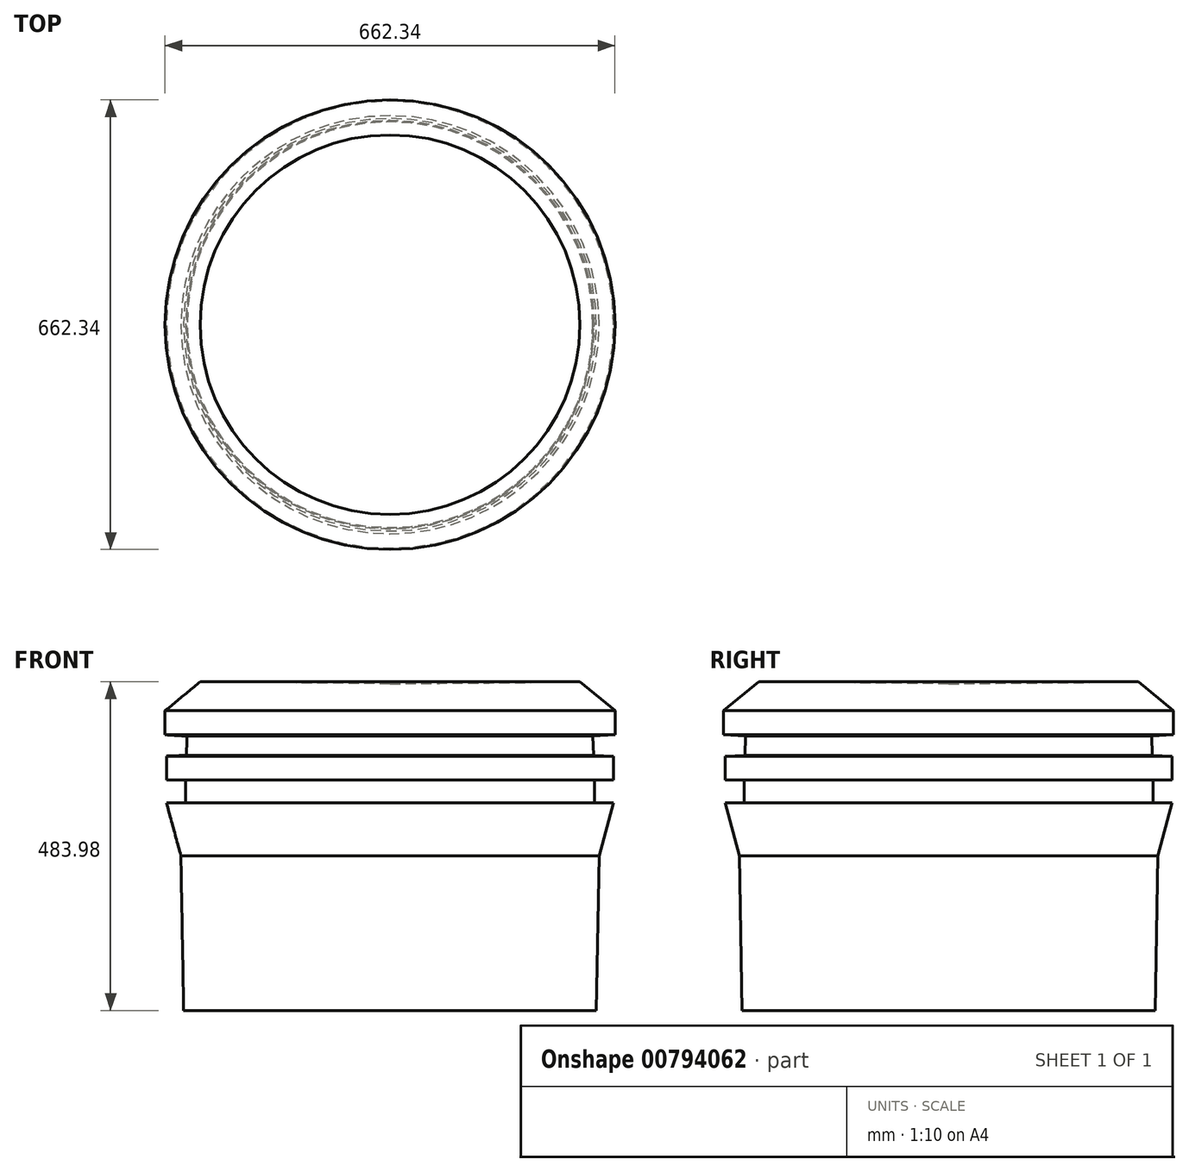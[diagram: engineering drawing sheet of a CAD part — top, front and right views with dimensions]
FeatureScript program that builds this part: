
annotation { "Feature Type Name" : "Feature", "Feature Type Description" : "" }
export const myFeature = defineFeature(function(context is Context, id is Id, definition is map)
    precondition{}
    {
        {
            var Q0;
            Q0=qCreatedBy(makeId("Front.planeOp"),FACE);
            var sketch = newSketch(context, id + "F0", { "sketchPlane" : qUnion([Q0])});
            skLineSegment(sketch, "E0", {"start": v(0, 0) * mm, "end": v(0, 295.8) * mm, "construction": true});
            skLineSegment(sketch, "E1", {"start": v(0, 0) * mm, "end": v(303.86, 0) * mm});
            skLineSegment(sketch, "E2", {"start": v(303.86, 0) * mm, "end": v(307.9, 228.01) * mm});
            skLineSegment(sketch, "E3", {"start": v(307.9, 228.01) * mm, "end": v(329.15, 305.92) * mm});
            skLineSegment(sketch, "E4", {"start": v(329.15, 305.92) * mm, "end": v(300.82, 305.92) * mm});
            skLineSegment(sketch, "E5", {"start": v(300.82, 305.92) * mm, "end": v(300.82, 339.3) * mm});
            skLineSegment(sketch, "E6", {"start": v(300.82, 339.3) * mm, "end": v(329.15, 339.3) * mm});
            skLineSegment(sketch, "E7", {"start": v(329.15, 339.3) * mm, "end": v(329.15, 374.71) * mm});
            skLineSegment(sketch, "E8", {"start": v(329.15, 374.71) * mm, "end": v(299.81, 375.73) * mm});
            skLineSegment(sketch, "E9", {"start": v(299.81, 375.73) * mm, "end": v(298.8, 404.05) * mm});
            skLineSegment(sketch, "E10", {"start": v(298.8, 404.05) * mm, "end": v(331.17, 406.08) * mm});
            skLineSegment(sketch, "E11", {"start": v(331.17, 406.08) * mm, "end": v(331.17, 441.49) * mm});
            skLineSegment(sketch, "E12", {"start": v(331.17, 441.49) * mm, "end": v(279.58, 483.98) * mm});
            skLineSegment(sketch, "E13", {"start": v(279.58, 483.98) * mm, "end": v(0, 481.2) * mm});
            skLineSegment(sketch, "E14", {"start": v(0, 0) * mm, "end": v(0, 481.2) * mm});
            skSolve(sketch);
        }
        {
            var Q0;
            Q0=makeQuery(id+"F0.imprint","IMPRINT",FACE,{"disambiguationData":[TD([[makeQuery(id+"F0.imprint","IMPRINT",EDGE,{"derivedFrom":sQuery(id+"F0.wireOp",EDGE,"E1")}),1.0]])]});
            var Q1;
            Q1=sQuery(id+"F0.wireOp",EDGE,"E14");
            revolve(context, id + "F1", {"surfaceOperationType" : NewSurfaceOperationType.NEW, "entities" : qUnion([Q0]), "axis" : qUnion([Q1]), "revolveType" : RevolveType.FULL});
        }
    });
